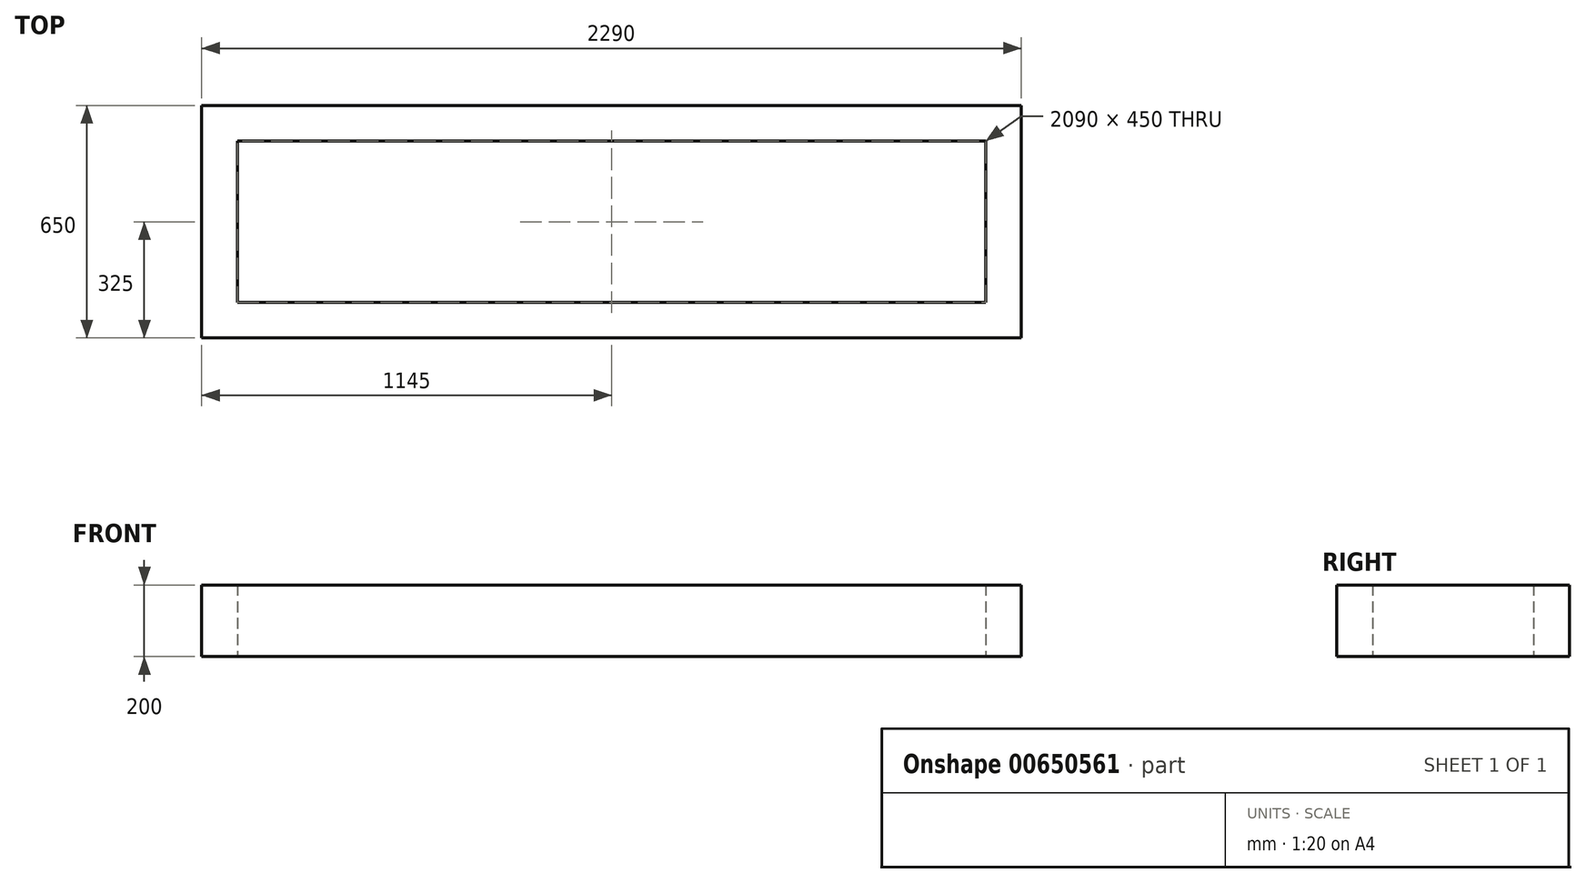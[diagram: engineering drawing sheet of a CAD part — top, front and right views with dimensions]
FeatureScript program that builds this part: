
annotation { "Feature Type Name" : "Feature", "Feature Type Description" : "" }
export const myFeature = defineFeature(function(context is Context, id is Id, definition is map)
    precondition{}
    {
        {
            var Q0;
            Q0=qCreatedBy(makeId("Top.planeOp"),FACE);
            var sketch = newSketch(context, id + "F0", { "sketchPlane" : qUnion([Q0]), "disableImprinting" : false});
            skLineSegment(sketch, "E0.bottom", {"start": v(0, 0) * mm, "end": v(-2290, 0) * mm});
            skLineSegment(sketch, "E0.top", {"start": v(0, 650) * mm, "end": v(-2290, 650) * mm});
            skLineSegment(sketch, "E0.left", {"start": v(0, 0) * mm, "end": v(0, 650) * mm});
            skLineSegment(sketch, "E0.right", {"start": v(-2290, 0) * mm, "end": v(-2290, 650) * mm});
            skLineSegment(sketch, "E1.bottom", {"start": v(-100, 100) * mm, "end": v(-2190, 100) * mm});
            skLineSegment(sketch, "E1.top", {"start": v(-100, 550) * mm, "end": v(-2190, 550) * mm});
            skLineSegment(sketch, "E1.left", {"start": v(-100, 100) * mm, "end": v(-100, 550) * mm});
            skLineSegment(sketch, "E1.right", {"start": v(-2190, 100) * mm, "end": v(-2190, 550) * mm});
            skSolve(sketch);
        }
        {
            var Q0;
            Q0=qSketchRegion(id+"F0",true);
            extrude(context, id + "F1", {"entities" : qUnion([Q0]), "depth" : 200 * mm, "offsetDistance" : 25 * mm});
        }
    });
